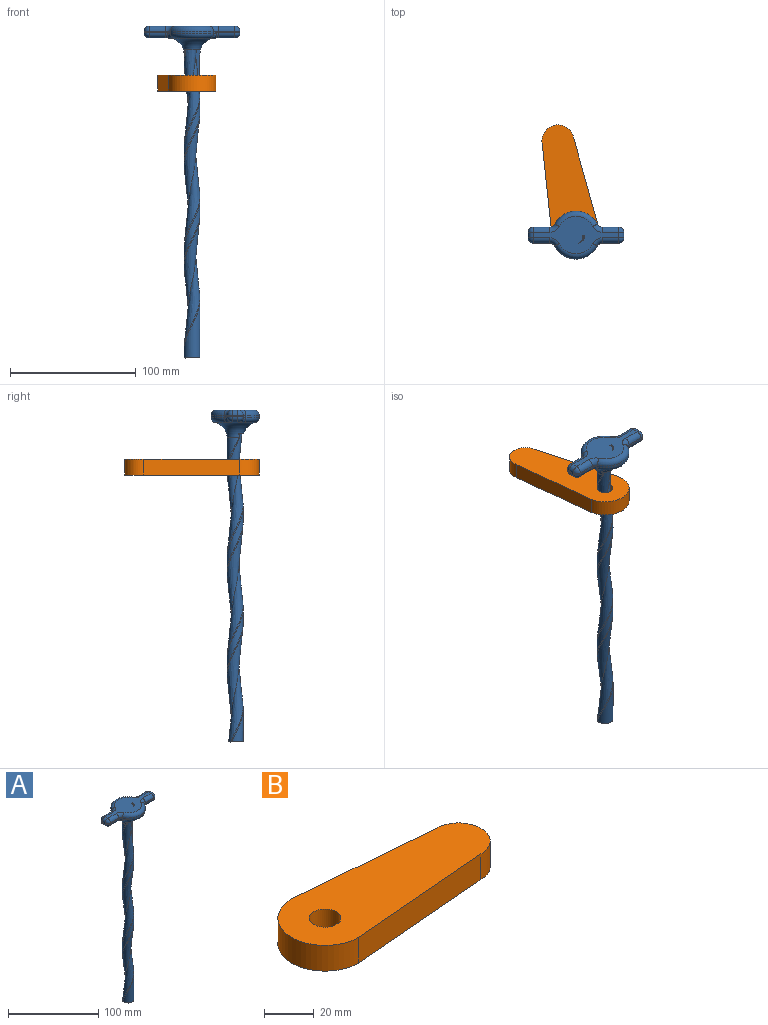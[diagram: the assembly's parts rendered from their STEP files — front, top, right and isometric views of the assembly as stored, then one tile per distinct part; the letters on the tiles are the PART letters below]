
ASSEMBLY  parts=2 mates=1
PART A: 66 faces, bbox 78.3x43.4x313.9 mm
  f0: plane 68.47x30.37mm, normal (0,0,1), area 885.3mm2, adj f24,f25,f30,f34,f35,f38,f39,f42
  f1: torus R=19.05mm, axis (0,0,1), area 1031mm2, adj f2,f3,f13,f21,f27,f31,f32,f37
  f2: plane 15.08x4.83mm, normal (0,0,-1), area 66.7mm2, adj f1,f15,f17,f20,f22,f28
  f3: cylinder r=6.35mm len=241.3mm, axis (0,0,-1), area 1957.8mm2, adj f1,f4,f58,f60,f63,f65
  f4: plane 14.81x13.57mm, normal (0,0,-1), area 102.6mm2, adj f3,f58,f59,f65
  f5: plane 13.3x1.27mm, normal (0,-1,0), area 16.9mm2, adj f46,f51,f54,f57
  f6: plane 4.45x1.27mm, normal (1,0,0), area 5.6mm2, adj f44,f52,f53,f57
  f7: plane 13.3x1.27mm, normal (0,1,0), area 16.9mm2, adj f36,f43,f44,f45
  f8: cylinder r=19.05mm len=33.99mm, axis (0,0,-1), area 74.9mm2, adj f26,f27,f35,f36
  f9: plane 13.3x1.27mm, normal (0,1,0), area 16.9mm2, adj f16,f17,f25,f26
  f10: plane 4.45x1.27mm, normal (-1,0,0), area 5.6mm2, adj f15,f16,f23,f24
  f11: plane 13.3x1.27mm, normal (0,-1,0), area 16.9mm2, adj f22,f23,f33,f34
  f12: cylinder r=19.05mm len=33.99mm, axis (0,0,-1), area 74.9mm2, adj f33,f37,f42,f46
  f13: plane 15.08x4.83mm, normal (0,0,-1), area 66.7mm2, adj f1,f40,f45,f50,f53,f54
  f14: sphere r=4.13mm, area 26.8mm2, adj f15,f16,f17
  f15: cylinder r=4.13mm len=4.45mm, axis (0,-1,0), area 28.8mm2, adj f2,f10,f14,f18
  f16: cylinder r=4.13mm len=4.13mm, axis (0,0,1), area 8.2mm2, adj f9,f10,f14,f19
  f17: cylinder r=4.13mm len=13.3mm, axis (-1,0,0), area 86.2mm2, adj f2,f9,f14,f20
  f18: sphere r=4.13mm, area 26.8mm2, adj f15,f22,f23
  f19: sphere r=4.13mm, area 17mm2, adj f16,f24,f25
  f20: torus R=8.26mm, axis (0,0,1), area 7.9mm2, adj f2,f17,f21,f26
  f21: bspline ~7.54x6.84mm, area 28.3mm2, adj f1,f20,f26,f27
  f22: cylinder r=4.13mm len=13.3mm, axis (1,0,0), area 86.2mm2, adj f2,f11,f18,f28
  f23: cylinder r=4.13mm len=4.13mm, axis (0,0,-1), area 8.2mm2, adj f10,f11,f18,f29
  f24: cylinder r=4.13mm len=4.45mm, axis (0,1,0), area 28.8mm2, adj f0,f10,f19,f29
  f25: cylinder r=4.13mm len=13.3mm, axis (1,0,0), area 86.2mm2, adj f0,f9,f19,f30
  f26: cylinder r=4.13mm len=3.68mm, axis (0,0,-1), area 6.7mm2, adj f8,f9,f20,f21,f30
  f27: torus R=14.92mm, axis (0,0,-1), area 215.9mm2, adj f1,f8,f21,f31
  f28: torus R=8.26mm, axis (0,0,1), area 7.9mm2, adj f2,f22,f32,f33
  f29: sphere r=4.13mm, area 26.8mm2, adj f23,f24,f34
  f30: torus R=8.26mm, axis (0,0,1), area 40.2mm2, adj f0,f25,f26,f35
  f31: bspline ~7.54x6.84mm, area 28.3mm2, adj f1,f27,f36,f40
  f32: bspline ~7.54x6.84mm, area 28.3mm2, adj f1,f28,f33,f37
  f33: cylinder r=4.13mm len=3.68mm, axis (0,0,-1), area 6.7mm2, adj f11,f12,f28,f32,f38
  f34: cylinder r=4.13mm len=13.3mm, axis (-1,0,0), area 86.2mm2, adj f0,f11,f29,f38
  f35: torus R=14.92mm, axis (0,0,1), area 250.7mm2, adj f0,f8,f30,f39
  f36: cylinder r=4.13mm len=3.68mm, axis (0,0,-1), area 6.7mm2, adj f7,f8,f31,f39,f40
  f37: torus R=14.92mm, axis (0,0,-1), area 215.9mm2, adj f1,f12,f32,f41
  f38: torus R=8.26mm, axis (0,0,1), area 40.2mm2, adj f0,f33,f34,f42
  f39: torus R=8.26mm, axis (0,0,1), area 40.2mm2, adj f0,f35,f36,f43
  f40: torus R=8.26mm, axis (0,0,1), area 7.9mm2, adj f13,f31,f36,f45
  f41: bspline ~7.54x6.84mm, area 28.3mm2, adj f1,f37,f46,f50
  f42: torus R=14.92mm, axis (0,0,1), area 250.7mm2, adj f0,f12,f38,f47
  f43: cylinder r=4.13mm len=13.3mm, axis (1,0,0), area 86.2mm2, adj f0,f7,f39,f48
  f44: cylinder r=4.13mm len=4.13mm, axis (0,0,-1), area 8.2mm2, adj f6,f7,f48,f49
  f45: cylinder r=4.13mm len=13.3mm, axis (-1,0,0), area 86.2mm2, adj f7,f13,f40,f49
  f46: cylinder r=4.13mm len=3.68mm, axis (0,0,-1), area 6.7mm2, adj f5,f12,f41,f47,f50
  f47: torus R=8.26mm, axis (0,0,1), area 40.2mm2, adj f0,f42,f46,f51
  f48: sphere r=4.13mm, area 26.8mm2, adj f43,f44,f52
  f49: sphere r=4.13mm, area 17mm2, adj f44,f45,f53
  f50: torus R=8.26mm, axis (0,0,1), area 7.9mm2, adj f13,f41,f46,f54
  f51: cylinder r=4.13mm len=13.3mm, axis (-1,0,0), area 86.2mm2, adj f0,f5,f47,f55
  f52: cylinder r=4.13mm len=4.45mm, axis (0,-1,0), area 28.8mm2, adj f0,f6,f48,f55
  f53: cylinder r=4.13mm len=4.45mm, axis (0,1,0), area 28.8mm2, adj f6,f13,f49,f56
  f54: cylinder r=4.13mm len=13.3mm, axis (1,0,0), area 86.2mm2, adj f5,f13,f50,f56
  f55: sphere r=4.13mm, area 17mm2, adj f51,f52,f57
  f56: sphere r=4.13mm, area 26.8mm2, adj f53,f54,f57
  f57: cylinder r=4.13mm len=4.13mm, axis (0,0,1), area 8.2mm2, adj f5,f6,f55,f56
  f58: plane 34.5x3.6mm, normal (0,1,0), area 59.8mm2, adj f3,f4,f61,f63
  f59: bspline ~273.73x12.48mm, area 2679.7mm2, adj f4,f60,f61,f65
  f60: plane 56.72x4.1mm, normal (0,-1,0), area 122.8mm2, adj f0,f1,f3,f59,f61,f62,f65
  f61: bspline ~279.4x13.69mm, area 2934.1mm2, adj f0,f58,f59,f60,f62,f63,f64
  f62: cylinder r=6.85mm len=18.7mm, axis (0,0,1), area 252.4mm2, adj f0,f1,f60,f61,f64
  f63: bspline ~210.82x12.75mm, area 216.3mm2, adj f3,f58,f61,f64
  f64: bspline ~4.82x1.68mm, area 3.8mm2, adj f1,f61,f62,f63
  f65: bspline ~209.58x12.75mm, area 216.3mm2, adj f3,f4,f59,f60
PART B: 7 faces, bbox 108x38.1x12.7 mm
  f0: plane 76.2x12.7mm, normal (0.08,1,0), area 971.1mm2, adj f1,f3,f5,f6
  f1: cylinder r=19.05mm len=38.1mm, axis (0,0,-1), area 760.1mm2, adj f0,f2,f5,f6
  f2: plane 76.2x12.7mm, normal (0.08,-1,0), area 971.1mm2, adj f1,f3,f5,f6
  f3: cylinder r=12.7mm len=25.4mm, axis (0,0,-1), area 506.7mm2, adj f0,f2,f5,f6
  f4: cylinder r=6.35mm len=12.7mm, axis (0,0,-1), area 506.7mm2, adj f5,f6
  f5: plane 107.95x38.1mm, normal (0,0,1), area 3116.1mm2, adj f0,f1,f2,f3,f4
  f6: plane 107.95x38.1mm, normal (0,0,-1), area 3116.1mm2, adj f0,f1,f2,f3,f4
PLACE A at identity fixed
PLACE B rot(axis=(0,0,1),100.8deg) t=(0,0,211.85)mm
MATE cylindrical A.f1 <-> B.f1  axis (0,0,-1) through (0,0,120.65)mm
